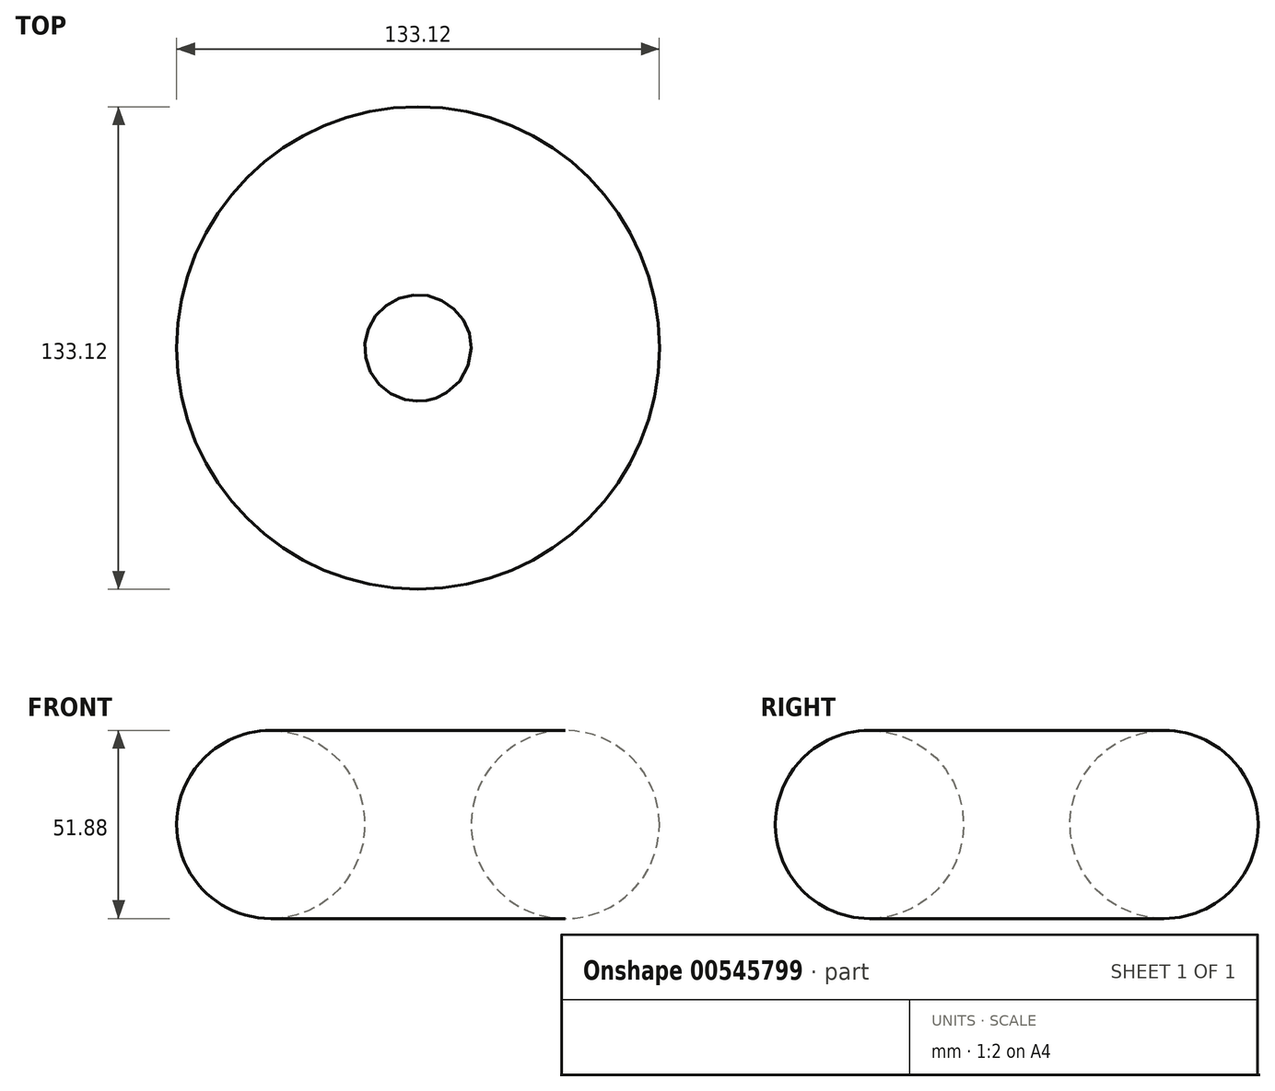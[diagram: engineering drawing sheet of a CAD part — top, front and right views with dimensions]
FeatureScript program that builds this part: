
annotation { "Feature Type Name" : "Feature", "Feature Type Description" : "" }
export const myFeature = defineFeature(function(context is Context, id is Id, definition is map)
    precondition{}
    {
        {
            var Q0;
            Q0=qCreatedBy(makeId("Front.planeOp"),FACE);
            var sketch = newSketch(context, id + "F0", { "sketchPlane" : qUnion([Q0])});
            skCircle(sketch, "E0", {"center": v(-40.62, 0) * mm, "radius": 25.94 * mm});
            skSolve(sketch);
        }
        {
            var Q0;
            Q0=qCreatedBy(makeId("Front.planeOp"),FACE);
            var sketch = newSketch(context, id + "F1", { "sketchPlane" : qUnion([Q0])});
            skLineSegment(sketch, "E1", {"start": v(0, 42.14) * mm, "end": v(0, -44.59) * mm});
            skSolve(sketch);
        }
        {
            var Q0;
            Q0=makeQuery(id+"F0.imprint","IMPRINT",FACE,{"disambiguationData":[TD([[makeQuery(id+"F0.imprint","IMPRINT",EDGE,{"derivedFrom":sQuery(id+"F0.wireOp",EDGE,"E0")}),1.0]])]});
            var Q1;
            Q1=sQuery(id+"F1.wireOp",EDGE,"E1");
            revolve(context, id + "F2", {"entities" : qUnion([Q0]), "axis" : qUnion([Q1]), "revolveType" : RevolveType.FULL});
        }
    });
